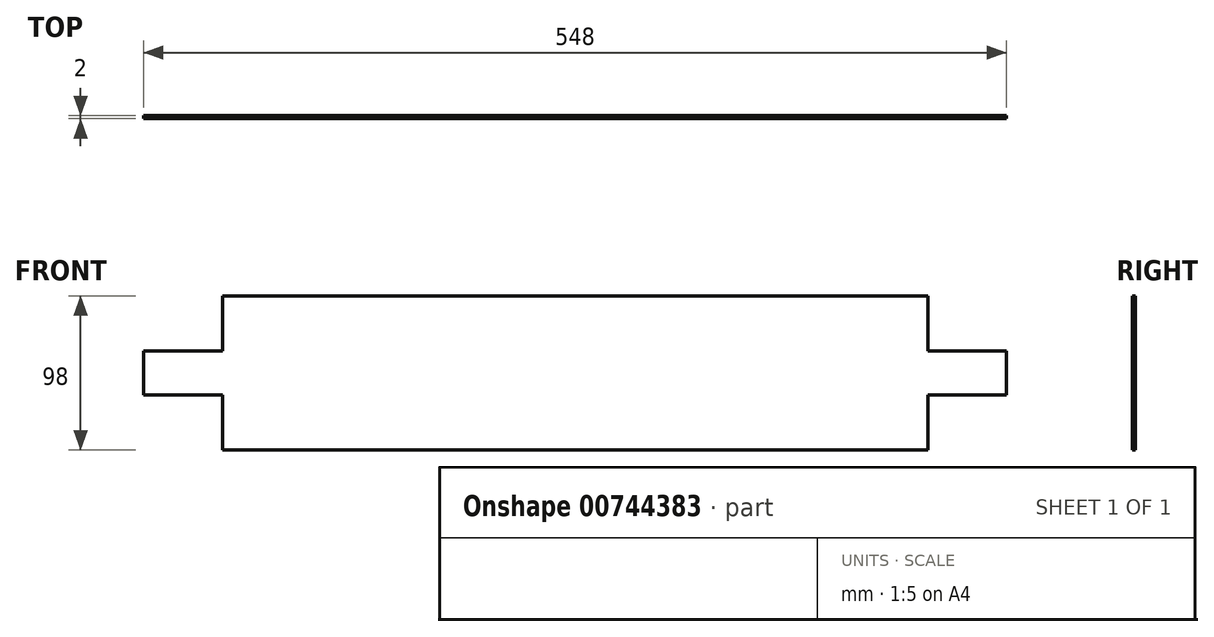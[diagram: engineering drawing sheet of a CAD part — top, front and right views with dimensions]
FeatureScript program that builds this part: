
annotation { "Feature Type Name" : "Feature", "Feature Type Description" : "" }
export const myFeature = defineFeature(function(context is Context, id is Id, definition is map)
    precondition{}
    {
        {
            var Q0;
            Q0=qCreatedBy(makeId("Front.planeOp"),FACE);
            var sketch = newSketch(context, id + "F0", { "sketchPlane" : qUnion([Q0])});
            skLineSegment(sketch, "E0.bottom", {"start": v(-224, -49) * mm, "end": v(224, -49) * mm});
            skLineSegment(sketch, "E0.top", {"start": v(-224, 49) * mm, "end": v(224, 49) * mm});
            skLineSegment(sketch, "E0.left", {"start": v(-224, -49) * mm, "end": v(-224, 49) * mm});
            skLineSegment(sketch, "E0.right", {"start": v(224, -49) * mm, "end": v(224, 49) * mm});
            skPoint(sketch, "E0.middle", {"position": v(0, 0) * mm});
            skLineSegment(sketch, "E1", {"start": v(224, 49) * mm, "end": v(224, 14) * mm});
            skLineSegment(sketch, "E2", {"start": v(224, 14) * mm, "end": v(-224, 14) * mm});
            skLineSegment(sketch, "E3", {"start": v(224, 14) * mm, "end": v(224, 35) * mm});
            skLineSegment(sketch, "E4", {"start": v(224, 35) * mm, "end": v(-224, 35) * mm});
            skLineSegment(sketch, "E5", {"start": v(224, 14) * mm, "end": v(224, -14) * mm});
            skLineSegment(sketch, "E6", {"start": v(224, -14) * mm, "end": v(-224, -14) * mm});
            skLineSegment(sketch, "E7", {"start": v(224, -49) * mm, "end": v(224, -28) * mm});
            skLineSegment(sketch, "E8", {"start": v(224, -28) * mm, "end": v(-224, -28) * mm});
            skLineSegment(sketch, "E9.bottom", {"start": v(224, -14) * mm, "end": v(274, -14) * mm});
            skLineSegment(sketch, "E9.top", {"start": v(224, 14) * mm, "end": v(274, 14) * mm});
            skLineSegment(sketch, "E9.left", {"start": v(224, -14) * mm, "end": v(224, 14) * mm});
            skLineSegment(sketch, "E9.right", {"start": v(274, -14) * mm, "end": v(274, 14) * mm});
            skLineSegment(sketch, "E10.bottom", {"start": v(-224, 14) * mm, "end": v(-224, 14) * mm});
            skLineSegment(sketch, "E10.top", {"start": v(-224, -14) * mm, "end": v(-224, -14) * mm});
            skLineSegment(sketch, "E10.left", {"start": v(-224, 14) * mm, "end": v(-224, -14) * mm});
            skLineSegment(sketch, "E10.right", {"start": v(-224, 14) * mm, "end": v(-224, -14) * mm});
            skLineSegment(sketch, "E11.bottom", {"start": v(-224, 14) * mm, "end": v(-274, 14) * mm});
            skLineSegment(sketch, "E11.top", {"start": v(-224, -14) * mm, "end": v(-274, -14) * mm});
            skLineSegment(sketch, "E11.right", {"start": v(-274, 14) * mm, "end": v(-274, -14) * mm});
            skSolve(sketch);
        }
        {
            var Q0;
            {var subQ0=sQuery(id+"F0.wireOp",EDGE,"E0.top");Q0=makeQuery(id+"F0.imprint","IMPRINT",FACE,{"disambiguationData":[TD([[makeQuery(id+"F0.imprint","IMPRINT",EDGE,{"derivedFrom":subQ0}),-1.0]])]});}
            var Q1;
            {var subQ0=sQuery(id+"F0.wireOp",EDGE,"E2");Q1=makeQuery(id+"F0.imprint","IMPRINT",FACE,{"disambiguationData":[TD([[makeQuery(id+"F0.imprint","IMPRINT",EDGE,{"derivedFrom":subQ0}),-1.0]])]});}
            var Q2;
            Q2=makeQuery(id+"F0.imprint","IMPRINT",FACE,{"disambiguationData":[TD([[makeQuery(id+"F0.imprint","IMPRINT",EDGE,{"derivedFrom":sQuery(id+"F0.wireOp",EDGE,"E2")}),1.0]])]});
            var Q3;
            Q3=makeQuery(id+"F0.imprint","IMPRINT",FACE,{"disambiguationData":[TD([[makeQuery(id+"F0.imprint","IMPRINT",EDGE,{"derivedFrom":sQuery(id+"F0.wireOp",EDGE,"E11.bottom")}),1.0]])]});
            var Q4;
            Q4=makeQuery(id+"F0.imprint","IMPRINT",FACE,{"disambiguationData":[TD([[makeQuery(id+"F0.imprint","IMPRINT",EDGE,{"derivedFrom":sQuery(id+"F0.wireOp",EDGE,"E0.right")}),1.0]])]});
            var Q5;
            {var subQ0=sQuery(id+"F0.wireOp",EDGE,"E0.bottom");Q5=makeQuery(id+"F0.imprint","IMPRINT",FACE,{"disambiguationData":[TD([[makeQuery(id+"F0.imprint","IMPRINT",EDGE,{"derivedFrom":subQ0}),1.0]])]});}
            var Q6;
            Q6=makeQuery(id+"F0.imprint","IMPRINT",FACE,{"disambiguationData":[TD([[makeQuery(id+"F0.imprint","IMPRINT",EDGE,{"derivedFrom":sQuery(id+"F0.wireOp",EDGE,"E9.bottom")}),1.0]])]});
            extrude(context, id + "F1", {"entities" : qUnion([Q0, Q1, Q2, Q3, Q4, Q5, Q6]), "depth" : 2 * mm, "offsetDistance" : 25 * mm});
        }
    });
